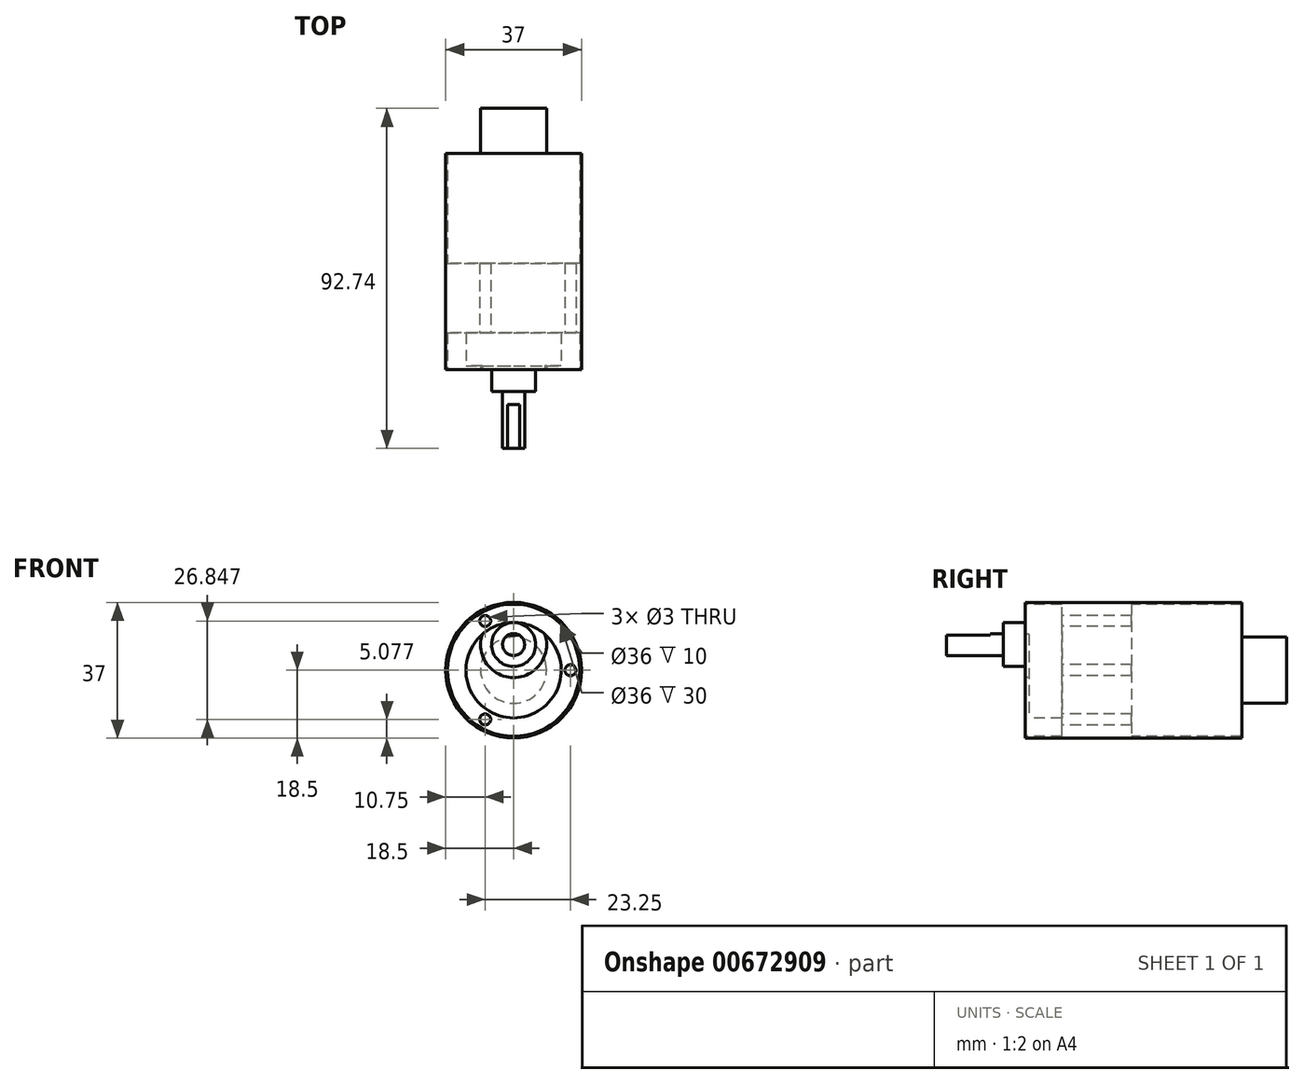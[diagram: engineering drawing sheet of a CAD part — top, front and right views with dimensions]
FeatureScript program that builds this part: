
annotation { "Feature Type Name" : "Feature", "Feature Type Description" : "" }
export const myFeature = defineFeature(function(context is Context, id is Id, definition is map)
    precondition{}
    {
        {
            var Q0;
            Q0=qCreatedBy(makeId("Front.planeOp"),FACE);
            var sketch = newSketch(context, id + "F0", { "sketchPlane" : qUnion([Q0])});
            skCircle(sketch, "E0", {"center": v(0, 0) * mm, "radius": 18.5 * mm});
            skCircle(sketch, "E1", {"center": v(0, 7) * mm, "radius": 6 * mm});
            skCircle(sketch, "E2", {"center": v(0, 0) * mm, "radius": 13 * mm});
            skCircle(sketch, "E3", {"center": v(-15.5, 0) * mm, "radius": 1.5 * mm});
            skCircle(sketch, "E4.MirrorC", {"center": v(15.5, 0) * mm, "radius": 1.5 * mm});
            skCircle(sketch, "E5.1.0", {"center": v(7.75, -13.42) * mm, "radius": 1.5 * mm});
            skCircle(sketch, "E5.1.1", {"center": v(-7.75, 13.42) * mm, "radius": 1.5 * mm});
            skCircle(sketch, "E5.2.0", {"center": v(7.75, 13.42) * mm, "radius": 1.5 * mm});
            skCircle(sketch, "E5.2.1", {"center": v(-7.75, -13.42) * mm, "radius": 1.5 * mm});
            skCircle(sketch, "E6", {"center": v(0, 7) * mm, "radius": 3 * mm});
            skCircle(sketch, "E7", {"center": v(0, 0) * mm, "radius": 18 * mm});
            skArc(sketch, "E8", {"start": v(-8.56, 9.79) * mm, "mid": v(0, -2) * mm, "end": v(8.56, 9.79) * mm});
            skSolve(sketch);
        }
        {
            var Q0;
            Q0=makeQuery(id+"F0.imprint","IMPRINT",FACE,{"disambiguationData":[TD([[makeQuery(id+"F0.imprint","IMPRINT",EDGE,{"derivedFrom":sQuery(id+"F0.wireOp",EDGE,"E0")}),1.0]])]});
            var Q1;
            Q1=makeQuery(id+"F0.imprint","IMPRINT",FACE,{"disambiguationData":[TD([[makeQuery(id+"F0.imprint","IMPRINT",EDGE,{"derivedFrom":sQuery(id+"F0.wireOp",EDGE,"E1")}),-1.0]])]});
            var Q2;
            Q2=makeQuery(id+"F0.imprint","IMPRINT",FACE,{"disambiguationData":[TD([[makeQuery(id+"F0.imprint","IMPRINT",EDGE,{"derivedFrom":sQuery(id+"F0.wireOp",EDGE,"E1")}),1.0]])]});
            var Q3;
            Q3=makeQuery(id+"F0.imprint","IMPRINT",FACE,{"disambiguationData":[TD([[makeQuery(id+"F0.imprint","IMPRINT",EDGE,{"derivedFrom":sQuery(id+"F0.wireOp",EDGE,"E3")}),1.0]])]});
            var Q4;
            Q4=makeQuery(id+"F0.imprint","IMPRINT",FACE,{"disambiguationData":[TD([[makeQuery(id+"F0.imprint","IMPRINT",EDGE,{"derivedFrom":sQuery(id+"F0.wireOp",EDGE,"E5.1.0")}),1.0]])]});
            var Q5;
            Q5=makeQuery(id+"F0.imprint","IMPRINT",FACE,{"disambiguationData":[TD([[makeQuery(id+"F0.imprint","IMPRINT",EDGE,{"derivedFrom":sQuery(id+"F0.wireOp",EDGE,"E4.MirrorC")}),-1.0]])]});
            var Q6;
            Q6=makeQuery(id+"F0.imprint","IMPRINT",FACE,{"disambiguationData":[TD([[makeQuery(id+"F0.imprint","IMPRINT",EDGE,{"derivedFrom":sQuery(id+"F0.wireOp",EDGE,"E5.2.0")}),1.0]])]});
            var Q7;
            Q7=makeQuery(id+"F0.imprint","IMPRINT",FACE,{"disambiguationData":[TD([[makeQuery(id+"F0.imprint","IMPRINT",EDGE,{"derivedFrom":sQuery(id+"F0.wireOp",EDGE,"E5.2.1")}),-1.0]])]});
            var Q8;
            Q8=makeQuery(id+"F0.imprint","IMPRINT",FACE,{"disambiguationData":[TD([[makeQuery(id+"F0.imprint","IMPRINT",EDGE,{"derivedFrom":sQuery(id+"F0.wireOp",EDGE,"E5.1.1")}),-1.0]])]});
            var Q9;
            Q9=makeQuery(id+"F0.imprint","IMPRINT",FACE,{"disambiguationData":[TD([[makeQuery(id+"F0.imprint","IMPRINT",EDGE,{"derivedFrom":sQuery(id+"F0.wireOp",EDGE,"E6")}),1.0]])]});
            var Q10;
            Q10=makeQuery(id+"F0.imprint","IMPRINT",FACE,{"disambiguationData":[TD([[makeQuery(id+"F0.imprint","IMPRINT",EDGE,{"derivedFrom":sQuery(id+"F0.wireOp",EDGE,"E2")}),-1.0]])]});
            var Q11;
            {var subQ0=sQuery(id+"F0.wireOp",EDGE,"E8");Q11=makeQuery(id+"F0.imprint","IMPRINT",FACE,{"disambiguationData":[TD([[makeQuery(id+"F0.imprint","IMPRINT",EDGE,{"derivedFrom":subQ0}),-1.0]])]});}
            extrude(context, id + "F1", {"entities" : qUnion([Q0, Q1, Q2, Q3, Q4, Q5, Q6, Q7, Q8, Q9, Q10, Q11]), "oppositeDirection" : true, "depth" : 29 * mm, "offsetDistance" : 25 * mm});
        }
        {
            var Q0;
            Q0=makeQuery(id+"F1.opExtrude","CAP_FACE",FACE,{"disambiguationData":[OSD([sQuery(id+"F0.wireOp",EDGE,"E0")])],"isStart":false});
            var sketch = newSketch(context, id + "F2", { "sketchPlane" : qUnion([Q0])});
            skCircle(sketch, "E9.0", {"center": v(0, 0) * mm, "radius": 18 * mm});
            skSolve(sketch);
        }
        {
            var Q0;
            Q0=makeQuery(id+"F2.imprint","IMPRINT",FACE,{"disambiguationData":[TD([[makeQuery(id+"F2.imprint","IMPRINT",EDGE,{"derivedFrom":sQuery(id+"F2.wireOp",EDGE,"E9.0")}),-1.0]])]});
            extrude(context, id + "F3", {"entities" : qUnion([Q0]), "operationType" : NewBodyOperationType.ADD, "depth" : 30 * mm, "offsetDistance" : 25 * mm});
        }
        {
            var Q0;
            Q0=makeQuery(id+"F3.opExtrude","CAP_FACE",FACE,{"disambiguationData":[OSD([sQuery(id+"F2.wireOp",EDGE,"E9.0")])],"isStart":false});
            var sketch = newSketch(context, id + "F4", { "sketchPlane" : qUnion([Q0])});
            skCircle(sketch, "E10", {"center": v(0, 0) * mm, "radius": 9 * mm});
            skSolve(sketch);
        }
        {
            var Q0;
            Q0=makeQuery(id+"F4.imprint","IMPRINT",FACE,{"disambiguationData":[TD([[makeQuery(id+"F4.imprint","IMPRINT",EDGE,{"derivedFrom":sQuery(id+"F4.wireOp",EDGE,"E10")}),1.0]])]});
            extrude(context, id + "F5", {"entities" : qUnion([Q0]), "operationType" : NewBodyOperationType.ADD, "depth" : 12.24 * mm, "offsetDistance" : 25 * mm});
        }
        {
            var Q0;
            Q0=makeQuery(id+"F0.imprint","IMPRINT",FACE,{"disambiguationData":[TD([[makeQuery(id+"F0.imprint","IMPRINT",EDGE,{"derivedFrom":sQuery(id+"F0.wireOp",EDGE,"E1")}),1.0]])]});
            extrude(context, id + "F6", {"entities" : qUnion([Q0]), "operationType" : NewBodyOperationType.ADD, "depth" : 6 * mm, "offsetDistance" : 25 * mm});
        }
        {
            var Q0;
            Q0=makeQuery(id+"F0.imprint","IMPRINT",FACE,{"disambiguationData":[TD([[makeQuery(id+"F0.imprint","IMPRINT",EDGE,{"derivedFrom":sQuery(id+"F0.wireOp",EDGE,"E6")}),1.0]])]});
            extrude(context, id + "F7", {"entities" : qUnion([Q0]), "operationType" : NewBodyOperationType.ADD, "depth" : (6 + 15.5) * mm, "offsetDistance" : 25 * mm});
        }
        {
            var Q0;
            Q0=makeQuery(id+"F0.imprint","IMPRINT",FACE,{"disambiguationData":[TD([[makeQuery(id+"F0.imprint","IMPRINT",EDGE,{"derivedFrom":sQuery(id+"F0.wireOp",EDGE,"E5.1.1")}),-1.0]])]});
            var Q1;
            Q1=makeQuery(id+"F0.imprint","IMPRINT",FACE,{"disambiguationData":[TD([[makeQuery(id+"F0.imprint","IMPRINT",EDGE,{"derivedFrom":sQuery(id+"F0.wireOp",EDGE,"E5.2.0")}),1.0]])]});
            var Q2;
            Q2=makeQuery(id+"F0.imprint","IMPRINT",FACE,{"disambiguationData":[TD([[makeQuery(id+"F0.imprint","IMPRINT",EDGE,{"derivedFrom":sQuery(id+"F0.wireOp",EDGE,"E4.MirrorC")}),-1.0]])]});
            var Q3;
            Q3=makeQuery(id+"F0.imprint","IMPRINT",FACE,{"disambiguationData":[TD([[makeQuery(id+"F0.imprint","IMPRINT",EDGE,{"derivedFrom":sQuery(id+"F0.wireOp",EDGE,"E5.2.1")}),-1.0]])]});
            var Q4;
            Q4=makeQuery(id+"F0.imprint","IMPRINT",FACE,{"disambiguationData":[TD([[makeQuery(id+"F0.imprint","IMPRINT",EDGE,{"derivedFrom":sQuery(id+"F0.wireOp",EDGE,"E3")}),1.0]])]});
            var Q5;
            Q5=makeQuery(id+"F0.imprint","IMPRINT",FACE,{"disambiguationData":[TD([[makeQuery(id+"F0.imprint","IMPRINT",EDGE,{"derivedFrom":sQuery(id+"F0.wireOp",EDGE,"E5.1.0")}),1.0]])]});
            extrude(context, id + "F8", {"entities" : qUnion([Q0, Q1, Q2, Q3, Q4, Q5]), "operationType" : NewBodyOperationType.REMOVE, "oppositeDirection" : true, "depth" : 10 * mm, "offsetDistance" : 25 * mm});
        }
        {
            var Q0;
            Q0=makeQuery(id+"F7.opExtrude","CAP_FACE",FACE,{"disambiguationData":[OSD([sQuery(id+"F0.wireOp",EDGE,"E6")])],"isStart":false});
            var sketch = newSketch(context, id + "F9", { "sketchPlane" : qUnion([Q0])});
            skCircle(sketch, "E11.0", {"center": v(0, 7) * mm, "radius": 3 * mm});
            skLineSegment(sketch, "E12.bottom", {"start": v(-7.35, 13.44) * mm, "end": v(6.01, 13.44) * mm});
            skLineSegment(sketch, "E12.top", {"start": v(-7.35, 9.5) * mm, "end": v(6.01, 9.5) * mm});
            skLineSegment(sketch, "E12.left", {"start": v(-7.35, 13.44) * mm, "end": v(-7.35, 9.5) * mm});
            skLineSegment(sketch, "E12.right", {"start": v(6.01, 13.44) * mm, "end": v(6.01, 9.5) * mm});
            skLineSegment(sketch, "E13", {"start": v(-3.45, 4) * mm, "end": v(3.7, 4) * mm});
            skSolve(sketch);
        }
        {
            var Q0;
            Q0=makeQuery(id+"F9.imprint","IMPRINT",FACE,{"disambiguationData":[TD([[makeQuery(id+"F9.imprint","IMPRINT",EDGE,{"derivedFrom":sQuery(id+"F9.wireOp",EDGE,"E12.bottom")}),-1.0]])]});
            var Q1;
            {var subQ0=sQuery(id+"F9.wireOp",EDGE,"E12.top");var subQ1=sQuery(id+"F9.wireOp",EDGE,"E11.0");var subQ2=makeQuery(id+"F9.imprint","INTERSECT",VERTEX,{"disambiguationData":[OD(0.0)],"derivedFrom":[subQ1,subQ0]});Q1=makeQuery(id+"F9.imprint","IMPRINT",FACE,{"disambiguationData":[TD([[makeQuery(id+"F9.imprint","IMPRINT",EDGE,{"disambiguationData":[TD([[subQ2,1.0]])],"derivedFrom":subQ1}),1.0]])]});}
            extrude(context, id + "F10", {"entities" : qUnion([Q0, Q1]), "operationType" : NewBodyOperationType.REMOVE, "oppositeDirection" : true, "depth" : 12 * mm, "offsetDistance" : 25 * mm});
        }
        {
            var Q0;
            {var subQ0=sQuery(id+"F0.wireOp",EDGE,"E8");Q0=makeQuery(id+"F0.imprint","IMPRINT",FACE,{"disambiguationData":[TD([[makeQuery(id+"F0.imprint","IMPRINT",EDGE,{"derivedFrom":subQ0}),-1.0]])]});}
            extrude(context, id + "F11", {"entities" : qUnion([Q0]), "operationType" : NewBodyOperationType.REMOVE, "oppositeDirection" : true, "depth" : 1 * mm, "offsetDistance" : 25 * mm});
        }
    });
